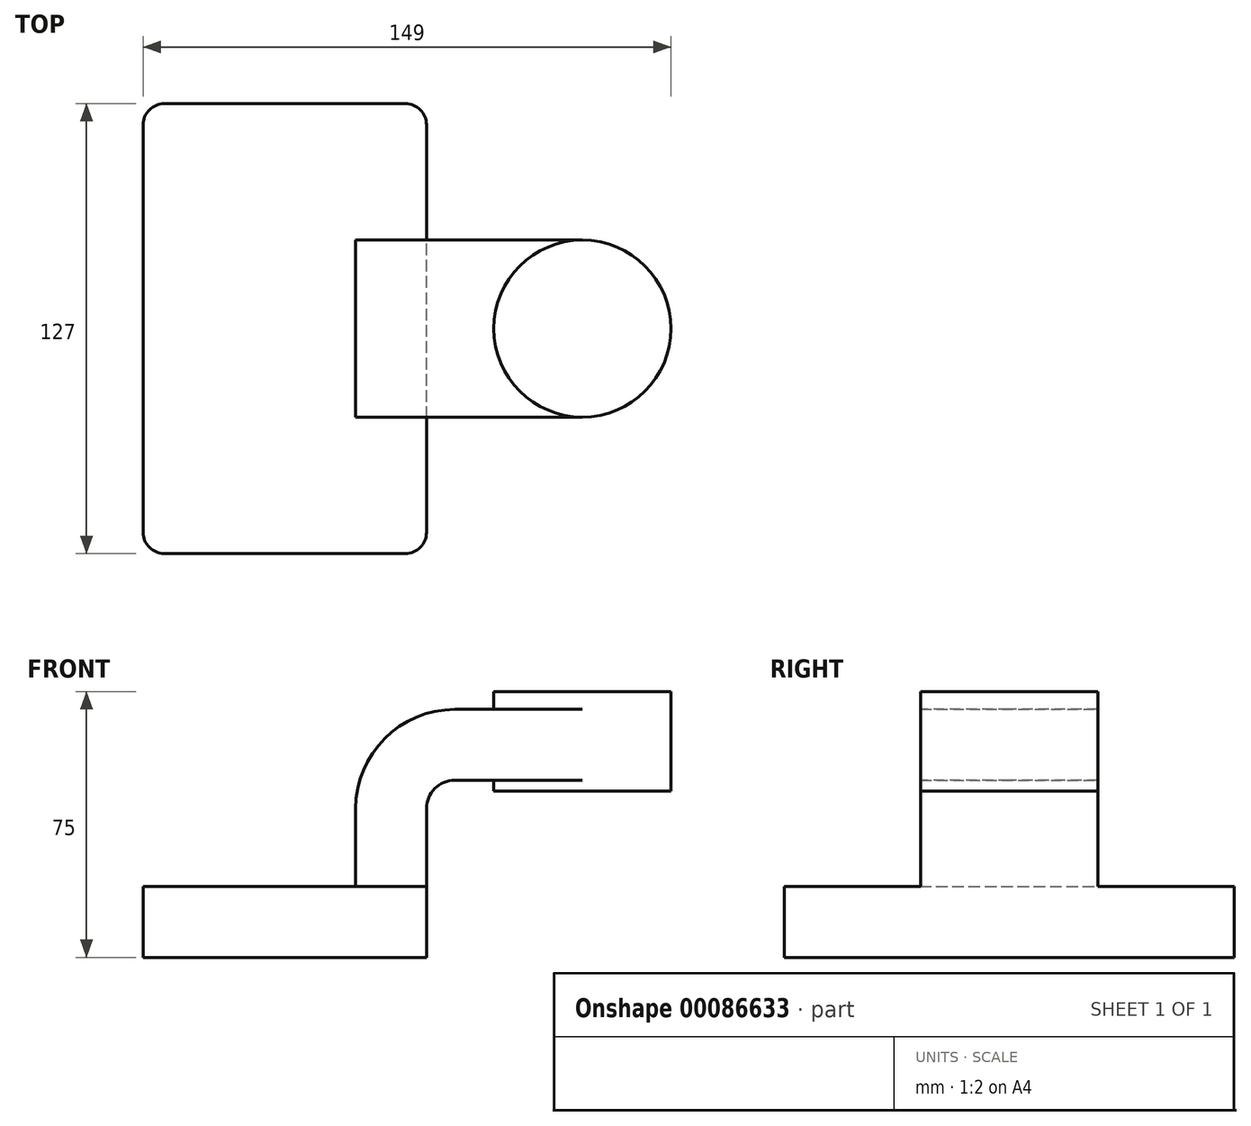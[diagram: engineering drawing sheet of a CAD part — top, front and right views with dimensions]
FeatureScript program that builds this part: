
annotation { "Feature Type Name" : "Feature", "Feature Type Description" : "" }
export const myFeature = defineFeature(function(context is Context, id is Id, definition is map)
    precondition{}
    {
        {
            var Q0;
            Q0=qCreatedBy(makeId("Front.planeOp"),FACE);
            var sketch = newSketch(context, id + "F0", { "sketchPlane" : qUnion([Q0])});
            skLineSegment(sketch, "E0.bottom", {"start": v(40, -10) * mm, "end": v(-40, -10) * mm});
            skLineSegment(sketch, "E0.top", {"start": v(40, 10) * mm, "end": v(-40, 10) * mm});
            skLineSegment(sketch, "E0.left", {"start": v(40, -10) * mm, "end": v(40, 10) * mm});
            skLineSegment(sketch, "E0.right", {"start": v(-40, -10) * mm, "end": v(-40, 10) * mm});
            skPoint(sketch, "E0.middle", {"position": v(0, 0) * mm});
            skLineSegment(sketch, "E1.bottom", {"start": v(109, 37) * mm, "end": v(59, 37) * mm});
            skLineSegment(sketch, "E1.top", {"start": v(109, 65) * mm, "end": v(59, 65) * mm});
            skLineSegment(sketch, "E1.left", {"start": v(109, 37) * mm, "end": v(109, 65) * mm});
            skLineSegment(sketch, "E1.right", {"start": v(59, 37) * mm, "end": v(59, 65) * mm});
            skPoint(sketch, "E1.middle", {"position": v(84, 51) * mm});
            skLineSegment(sketch, "E2", {"start": v(40, 10) * mm, "end": v(40, 32) * mm});
            skArc(sketch, "E3", {"start": v(40, 32) * mm, "mid": v(42.34, 37.66) * mm, "end": v(48, 40) * mm});
            skLineSegment(sketch, "E4", {"start": v(48, 40) * mm, "end": v(84, 40) * mm});
            skLineSegment(sketch, "E5.0", {"start": v(48, 60) * mm, "end": v(84, 60) * mm});
            skArc(sketch, "E5.1", {"start": v(20, 32) * mm, "mid": v(28.2, 51.8) * mm, "end": v(48, 60) * mm});
            skLineSegment(sketch, "E5.2", {"start": v(20, 10) * mm, "end": v(20, 32) * mm});
            skLineSegment(sketch, "E6", {"start": v(84, 37) * mm, "end": v(84, 65) * mm});
            skFitSpline(sketch, "E7", {"points": [v(-40, 10) * mm, v(48, 60) * mm], "startDerivative": vector(0, 60.59) * mm, "endDerivative": vector(147.88, 0) * mm});
            skSolve(sketch);
        }
        {
            var Q0;
            Q0=makeQuery(id+"F0.imprint","IMPRINT",FACE,{"disambiguationData":[TD([[makeQuery(id+"F0.imprint","IMPRINT",EDGE,{"derivedFrom":sQuery(id+"F0.wireOp",EDGE,"E0.bottom")}),-1.0]])]});
            extrude(context, id + "F1", {"entities" : qUnion([Q0]), "endBound" : BoundingType.SYMMETRIC, "depth" : 127 * mm});
        }
        {
            var Q0;
            {var subQ1=sQuery(id+"F0.wireOp",EDGE,"E2");Q0=makeQuery(id+"F0.imprint","IMPRINT",FACE,{"disambiguationData":[TD([[makeQuery(id+"F0.imprint","IMPRINT",EDGE,{"derivedFrom":subQ1}),1.0]])]});}
            var Q1;
            {var subQ0=sQuery(id+"F0.wireOp",EDGE,"E4");var subQ1=sQuery(id+"F0.wireOp",EDGE,"E1.right");var subQ2=makeQuery(id+"F0.imprint","INTERSECT",VERTEX,{"derivedFrom":[subQ1,subQ0]});Q1=makeQuery(id+"F0.imprint","IMPRINT",FACE,{"disambiguationData":[TD([[makeQuery(id+"F0.imprint","IMPRINT",EDGE,{"disambiguationData":[TD([[subQ2,-1.0]])],"derivedFrom":subQ1}),-1.0]])]});}
            extrude(context, id + "F2", {"entities" : qUnion([Q0, Q1]), "operationType" : NewBodyOperationType.ADD, "endBound" : BoundingType.SYMMETRIC, "depth" : 50 * mm});
        }
        {
            var Q0;
            Q0=makeQuery(id+"F0.imprint","IMPRINT",FACE,{"disambiguationData":[TD([[makeQuery(id+"F0.imprint","IMPRINT",EDGE,{"derivedFrom":sQuery(id+"F0.wireOp",EDGE,"E5.1")}),1.0]])]});
            extrude(context, id + "F3", {"entities" : qUnion([Q0]), "operationType" : NewBodyOperationType.ADD, "endBound" : BoundingType.SYMMETRIC, "depth" : 30 * mm});
        }
        {
            var Q0;
            {var subQ0=sQuery(id+"F0.wireOp",EDGE,"E1.left");Q0=makeQuery(id+"F0.imprint","IMPRINT",FACE,{"disambiguationData":[TD([[makeQuery(id+"F0.imprint","IMPRINT",EDGE,{"derivedFrom":subQ0}),1.0]])]});}
            var Q1;
            Q1=sQuery(id+"F0.wireOp",EDGE,"E6");
            revolve(context, id + "F4", {"operationType" : NewBodyOperationType.ADD, "entities" : qUnion([Q0]), "axis" : qUnion([Q1]), "revolveType" : RevolveType.FULL});
        }
        {
            var Q0;
            Q0=makeQuery(id+"F1.opExtrude","CAP_EDGE",EDGE,{"disambiguationData":[OSD([sQuery(id+"F0.wireOp",EDGE,"E0.right")])],"isStart":false});
            var Q1;
            Q1=makeQuery(id+"F1.opExtrude","CAP_EDGE",EDGE,{"disambiguationData":[OSD([sQuery(id+"F0.wireOp",EDGE,"E0.left")])],"isStart":false});
            var Q2;
            Q2=makeQuery(id+"F1.opExtrude","CAP_EDGE",EDGE,{"disambiguationData":[OSD([sQuery(id+"F0.wireOp",EDGE,"E0.left")])],"isStart":true});
            var Q3;
            Q3=makeQuery(id+"F1.opExtrude","CAP_EDGE",EDGE,{"disambiguationData":[OSD([sQuery(id+"F0.wireOp",EDGE,"E0.right")])],"isStart":true});
            fillet(context, id + "F5", {"entities" : qUnion([Q0, Q1, Q2, Q3]), "radius" : 6 * mm, "tangentPropagation" : true, "allowEdgeOverflow" : false});
        }
    });
